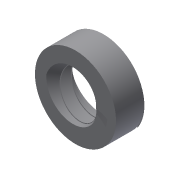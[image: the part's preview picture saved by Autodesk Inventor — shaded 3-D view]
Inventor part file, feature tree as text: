
AUTODESK INVENTOR PART (.ipt)
format: ipt  version: 2019.4 (Build 234330000, 330)  size: 410,112 bytes
history: native  units: mm
features: sketch x5, other x3, extrude x2, reference x2, sweep x1, revolve x1, pattern_circular x1, projected_geometry x1
ambient origin geometry x8: Origin, YZ Plane, XZ Plane, XY Plane, X Axis, Y Axis, Z Axis, Center Point
bodies: Solid1 (feature_tree)
feature tree (16):
  sweep  "Sweep1"
  extrude  "Extrusion1"  Depth=13.356687mm
  revolve  "Revolution1"  [1 undecoded]
  extrude  "Extrusion2"  Depth=2.0mm TaperAngle=0.0deg
  pattern_circular  "Circular Pattern1"  Count=8 Angle=360.0deg
  sketch  "Sketch1"  dims[d0=1.8mm d1=0.0mm d2=14.0mm d3=1.8mm d4=80.0mm d5=9.0mm d6=0.0mm d7=0.0mm]
  reference  "Reference1"
  reference  "Reference2"
  sketch  "3D Sketch1"
  other  "Helical Curve1"
  sketch  "Sketch2"  dims[d8=14.0mm d9=0.0mm d10=13.356687mm]
  sketch  "Sketch3"  dims[d12=90.0deg d13=2.0mm]
  projected_geometry  "Projected Loop1"
  sketch  "Sketch4"  dims[d14=2.0mm d15=14.0mm d16=0.0mm d17=80.0mm d18=360.0deg d20=6.678343mm d21=1.79mm d22=0.5mm d23=0.0mm d24=0.5mm]
  other  "Assembly_Motorcoupling_Nema_M3_Selfcentering.iam"
  other  "00_coupler_5_3_nema_screw:1"
note: 1 required parameter value undecoded (feature->parameter linkage not recoverable at this tier; creation-order binding heuristic only, values carry confidence <= 0.55)
